# Revit family: Double Louvered Door
name_source: partatom
category: Doors
revit_build: Autodesk Revit 2013 (Build: 20120716_1115(x64)
units: mm (PartAtom-declared; Revit-internal decimal feet)

## types (1)
- 800mm x 2100mm
    Analytic Construction = Metal
    Blade Angle = 70.00°
    Blade Count = 30
    Blade Depth = 80 mm  [stored 0.262467 ft]
    Blade Material = Oak Flooring
    Construction Type Id = MDOOR
    Door Panel Kickboard Height = 150 mm  [stored 0.492126 ft]
    Function = Interior
    Heat Transfer Coefficient (U) = 3.7021 W/(m²·K)
    Height = 2100 mm  [stored 6.88976 ft]
    Solar Heat Gain Coefficient = 0
    Thermal Resistance (R) = 0.2701 (m²·K)/W
    Thickness = 50 mm  [stored 0.164042 ft]
    Trim Projection Ext = 25 mm  [stored 0.082021 ft]
    Trim Projection Int = 25 mm  [stored 0.082021 ft]
    Trim Width = 76 mm
    Visual Light Transmittance = 0
    Wall Closure = By host

note: [stored X ft] marks values corroborated as IEEE doubles in the binary element streams (Revit-internal decimal feet)

## geometry (parser evidence)
native form markers: Blend x4, Sweep x9
no freeform markers — native parametric forms only
